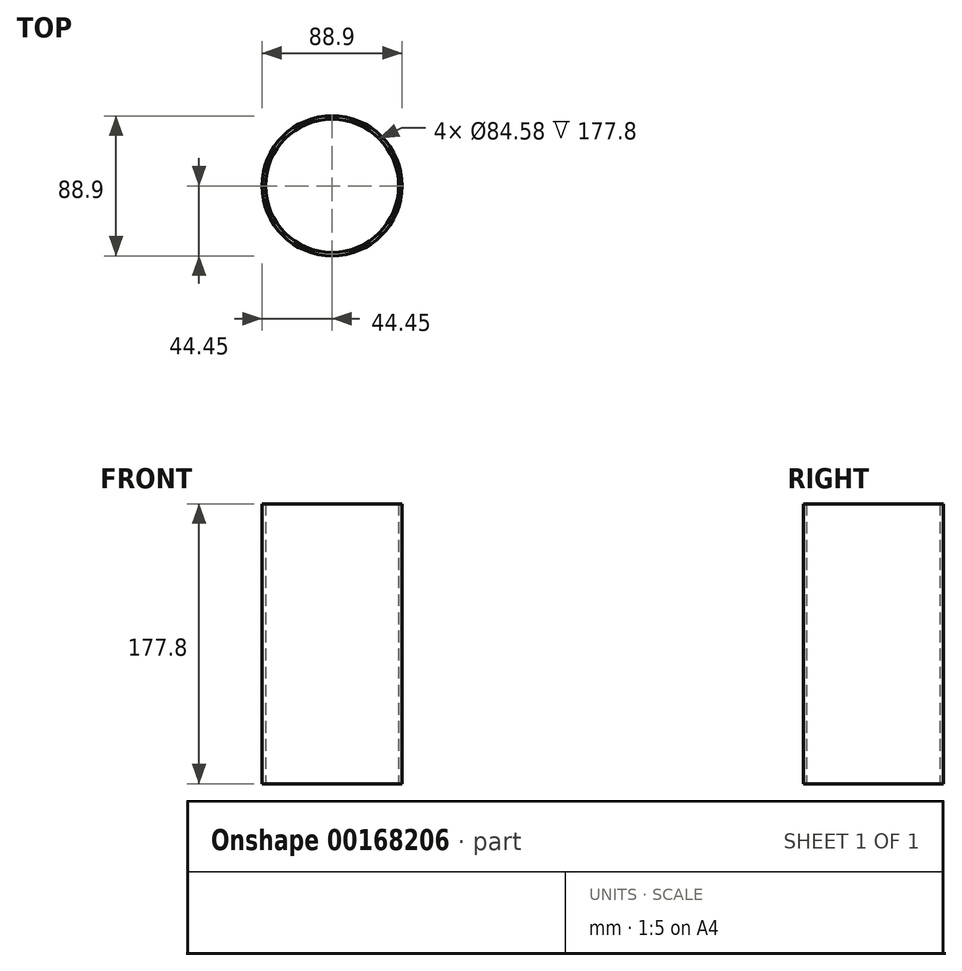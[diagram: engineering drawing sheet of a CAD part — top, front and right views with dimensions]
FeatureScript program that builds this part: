
annotation { "Feature Type Name" : "Feature", "Feature Type Description" : "" }
export const myFeature = defineFeature(function(context is Context, id is Id, definition is map)
    precondition{}
    {
        {
            var Q0;
            Q0=qCreatedBy(makeId("Top.planeOp"),FACE);
            var sketch = newSketch(context, id + "F0", { "sketchPlane" : qUnion([Q0])});
            skCircle(sketch, "E0", {"center": v(0, 0) * mm, "radius": 42.3 * mm});
            skCircle(sketch, "E1", {"center": v(0, 0) * mm, "radius": 44.45 * mm});
            skSolve(sketch);
        }
        {
            var Q0;
            Q0=qSketchRegion(id+"F0",true);
            extrude(context, id + "F1", {"entities" : qUnion([Q0]), "depth" : 177.8 * mm});
        }
    });
